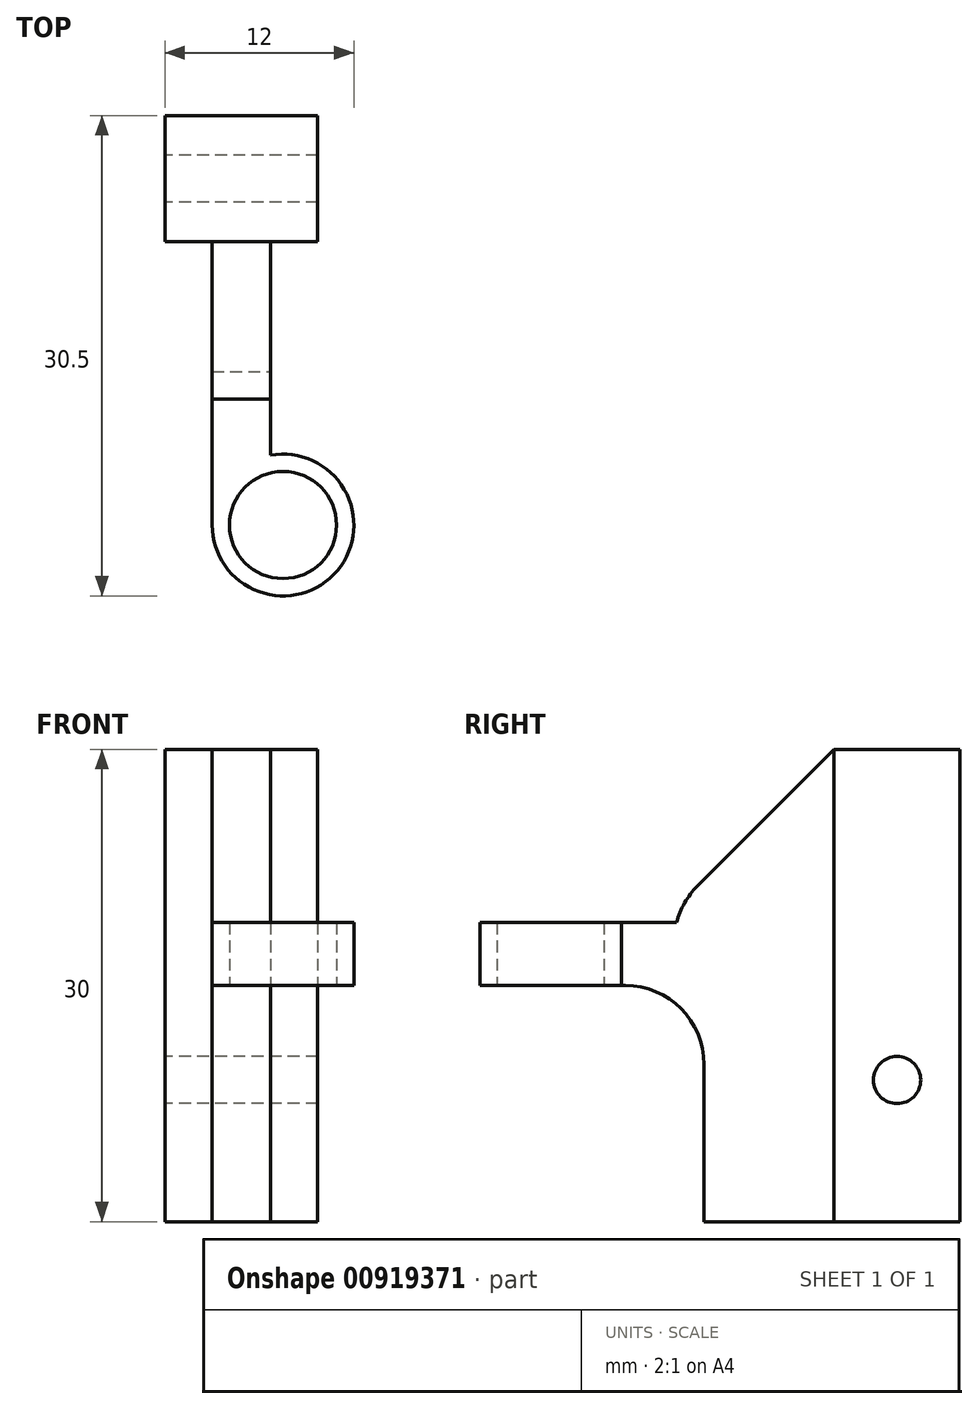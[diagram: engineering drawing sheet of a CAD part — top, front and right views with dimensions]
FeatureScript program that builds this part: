
annotation { "Feature Type Name" : "Feature", "Feature Type Description" : "" }
export const myFeature = defineFeature(function(context is Context, id is Id, definition is map)
    precondition{}
    {
        {
            var Q0;
            Q0=qCreatedBy(makeId("Top.planeOp"),FACE);
            var sketch = newSketch(context, id + "F0", { "sketchPlane" : qUnion([Q0])});
            skLineSegment(sketch, "E0", {"start": v(0, 0) * mm, "end": v(4, 0) * mm});
            skLineSegment(sketch, "E1", {"start": v(4, 0) * mm, "end": v(4, 4.5) * mm});
            skCircle(sketch, "E2", {"center": v(4, 4.5) * mm, "radius": 4.5 * mm});
            skLineSegment(sketch, "E3", {"start": v(-0.5, 4.5) * mm, "end": v(-0.5, 22.5) * mm});
            skLineSegment(sketch, "E4", {"start": v(-0.5, 22.5) * mm, "end": v(-3.5, 22.5) * mm});
            skLineSegment(sketch, "E5", {"start": v(-3.5, 22.5) * mm, "end": v(-3.5, 30.5) * mm});
            skLineSegment(sketch, "E6", {"start": v(-3.5, 30.5) * mm, "end": v(6.2, 30.5) * mm});
            skLineSegment(sketch, "E7", {"start": v(6.2, 30.5) * mm, "end": v(6.2, 22.5) * mm});
            skLineSegment(sketch, "E8", {"start": v(6.2, 22.5) * mm, "end": v(3.2, 22.5) * mm});
            skLineSegment(sketch, "E9", {"start": v(3.2, 22.5) * mm, "end": v(3.2, 8.93) * mm});
            skSolve(sketch);
        }
        {
            var Q0;
            Q0 = qSketchRegion(id + "F0", true);
            extrude(context, id + "F1", {"entities" : qUnion([Q0]), "depth" : 19 * mm, "offsetDistance" : 25 * mm});
        }
        {
            var Q0;
            Q0=makeQuery(id+"F1.opExtrude","CAP_FACE",FACE,{"disambiguationData":[OSD([sQuery(id+"F0.wireOp",EDGE,"E2"),sQuery(id+"F0.wireOp",EDGE,"E3"),sQuery(id+"F0.wireOp",EDGE,"E4"),sQuery(id+"F0.wireOp",EDGE,"E5"),sQuery(id+"F0.wireOp",EDGE,"E6"),sQuery(id+"F0.wireOp",EDGE,"E7"),sQuery(id+"F0.wireOp",EDGE,"E8"),sQuery(id+"F0.wireOp",EDGE,"E9")])],"isStart":false});
            var sketch = newSketch(context, id + "F2", { "sketchPlane" : qUnion([Q0])});
            skLineSegment(sketch, "E10", {"start": v(-3.5, 30.5) * mm, "end": v(-3.5, 22.5) * mm});
            skLineSegment(sketch, "E11", {"start": v(-3.5, 22.5) * mm, "end": v(-0.5, 22.5) * mm});
            skLineSegment(sketch, "E12", {"start": v(-0.5, 22.5) * mm, "end": v(-0.5, 12.5) * mm});
            skLineSegment(sketch, "E13", {"start": v(-0.5, 12.5) * mm, "end": v(3.2, 12.5) * mm});
            skLineSegment(sketch, "E14", {"start": v(3.2, 12.5) * mm, "end": v(3.2, 22.5) * mm});
            skLineSegment(sketch, "E15", {"start": v(3.2, 22.5) * mm, "end": v(6.2, 22.5) * mm});
            skLineSegment(sketch, "E16", {"start": v(6.2, 22.5) * mm, "end": v(6.2, 30.5) * mm});
            skLineSegment(sketch, "E17", {"start": v(6.2, 30.5) * mm, "end": v(-3.5, 30.5) * mm});
            skSolve(sketch);
        }
        {
            var Q0;
            Q0 = qSketchRegion(id + "F2", true);
            extrude(context, id + "F3", {"entities" : qUnion([Q0]), "operationType" : NewBodyOperationType.ADD, "depth" : 11 * mm, "offsetDistance" : 25 * mm});
        }
        {
            var Q0;
            Q0=makeQuery(id+"F1.opExtrude","CAP_FACE",FACE,{"disambiguationData":[OSD([sQuery(id+"F0.wireOp",EDGE,"E2"),sQuery(id+"F0.wireOp",EDGE,"E3"),sQuery(id+"F0.wireOp",EDGE,"E4"),sQuery(id+"F0.wireOp",EDGE,"E5"),sQuery(id+"F0.wireOp",EDGE,"E6"),sQuery(id+"F0.wireOp",EDGE,"E7"),sQuery(id+"F0.wireOp",EDGE,"E8"),sQuery(id+"F0.wireOp",EDGE,"E9")])],"isStart":true});
            var sketch = newSketch(context, id + "F4", { "sketchPlane" : qUnion([Q0])});
            skCircle(sketch, "E18", {"center": v(4, -4.5) * mm, "radius": 3.4 * mm});
            skSolve(sketch);
        }
        {
            var Q0;
            Q0 = qSketchRegion(id + "F4", true);
            extrude(context, id + "F5", {"entities" : qUnion([Q0]), "operationType" : NewBodyOperationType.REMOVE, "oppositeDirection" : true, "depth" : 25 * mm, "offsetDistance" : 25 * mm});
        }
        {
            var Q0;
            Q0=qCreatedBy(makeId("Top.planeOp"),FACE);
            var sketch = newSketch(context, id + "F6", { "sketchPlane" : qUnion([Q0])});
            skLineSegment(sketch, "E19", {"start": v(0, 0) * mm, "end": v(4.15, 0) * mm});
            skLineSegment(sketch, "E20", {"start": v(4.15, 0) * mm, "end": v(5.45, 0) * mm});
            skLineSegment(sketch, "E21", {"start": v(9.25, 9.05) * mm, "end": v(9.25, 0) * mm});
            skLineSegment(sketch, "E22", {"start": v(9.25, 0) * mm, "end": v(5.45, 0) * mm});
            skLineSegment(sketch, "E23", {"start": v(4.15, 0) * mm, "end": v(-2.95, 0) * mm});
            skLineSegment(sketch, "E24", {"start": v(-2.95, 0) * mm, "end": v(-2.95, 14.24) * mm});
            skLineSegment(sketch, "E25", {"start": v(-2.95, 14.24) * mm, "end": v(9.25, 14.24) * mm});
            skLineSegment(sketch, "E26", {"start": v(9.25, 14.24) * mm, "end": v(9.25, 9.05) * mm});
            skSolve(sketch);
        }
        {
            var Q0;
            Q0=makeQuery(id+"F3.boolean.opBoolean","MERGE",FACE,{"derivedFrom":[makeQuery(id+"F1.opExtrude","SWEPT_FACE",FACE,{"disambiguationData":[OSD([sQuery(id+"F0.wireOp",EDGE,"E5")])]}),makeQuery(id+"F3.opExtrude","SWEPT_FACE",FACE,{"disambiguationData":[OSD([sQuery(id+"F2.wireOp",EDGE,"E10")])]})]});
            var sketch = newSketch(context, id + "F7", { "sketchPlane" : qUnion([Q0])});
            skLineSegment(sketch, "E27", {"start": v(-26.5, 0) * mm, "end": v(-26.5, 9) * mm});
            skCircle(sketch, "E28", {"center": v(-26.5, 9) * mm, "radius": 1.5 * mm});
            skSolve(sketch);
        }
        {
            var Q0;
            Q0 = qSketchRegion(id + "F7", true);
            extrude(context, id + "F8", {"entities" : qUnion([Q0]), "operationType" : NewBodyOperationType.REMOVE, "oppositeDirection" : true, "depth" : 25 * mm, "offsetDistance" : 25 * mm});
        }
        {
            var Q0;
            Q0=makeQuery(id+"F3.opExtrude","CAP_EDGE",EDGE,{"disambiguationData":[OSD([sQuery(id+"F2.wireOp",EDGE,"E13")])],"isStart":false});
            chamfer(context, id + "F9", {"entities" : qUnion([Q0]), "width" : 10 * mm, "tangentPropagation" : true});
        }
        {
            var Q0;
            Q0 = qSketchRegion(id + "F6", true);
            extrude(context, id + "F10", {"entities" : qUnion([Q0]), "operationType" : NewBodyOperationType.REMOVE, "depth" : 15 * mm, "offsetDistance" : 25 * mm});
        }
        {
            var Q0;
            {var subQ0=sQuery(id+"F2.wireOp",EDGE,"E13");Q0=makeQuery(id+"F9.opChamfer","BLEND_EDGE",EDGE,{"blendedFrom":[makeQuery(id+"F3.opExtrude","CAP_EDGE",EDGE,{"disambiguationData":[OSD([subQ0])],"isStart":false}),makeQuery(id+"F3.opExtrude","SWEPT_FACE",FACE,{"disambiguationData":[OSD([subQ0])]})],"blendedInto":[makeQuery(id+"F3.opExtrude","SWEPT_FACE",FACE,{"disambiguationData":[OSD([subQ0])]})]});}
            var Q1;
            Q1=makeQuery(id+"F10.boolean.opBoolean","COPY",EDGE,{"derivedFrom":makeQuery(id+"F10.opExtrude","CAP_EDGE",EDGE,{"disambiguationData":[OSD([sQuery(id+"F6.wireOp",EDGE,"E25")])],"isStart":false})});
            fillet(context, id + "F11", {"entities" : qUnion([Q0, Q1]), "radius" : 5 * mm, "tangentPropagation" : true, "allowEdgeOverflow" : false});
        }
    });
